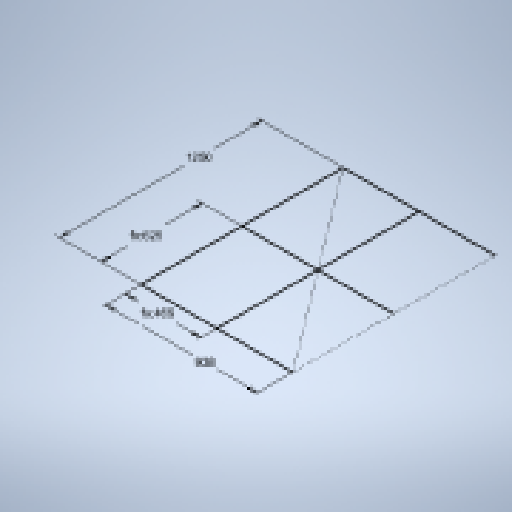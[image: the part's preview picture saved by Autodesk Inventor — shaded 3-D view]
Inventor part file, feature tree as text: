
AUTODESK INVENTOR PART (.ipt)
format: ipt  version: 2025 (Build 290162010, 162A)  size: 134,144 bytes
history: native  units: in
note: dims shown in document units (in); Inventor stores cm internally (conversion verified against a paired STEP export)
features: sketch x1
ambient origin geometry x8: Origin, YZ Plane, XZ Plane, XY Plane, X Axis, Y Axis, Z Axis, Center Point
feature tree (1):
  sketch  "Sketch3"  dims[d7=36.9291in d8=49.2126in d23=24.6063in d24=18.4646in d25=49.2126in]
